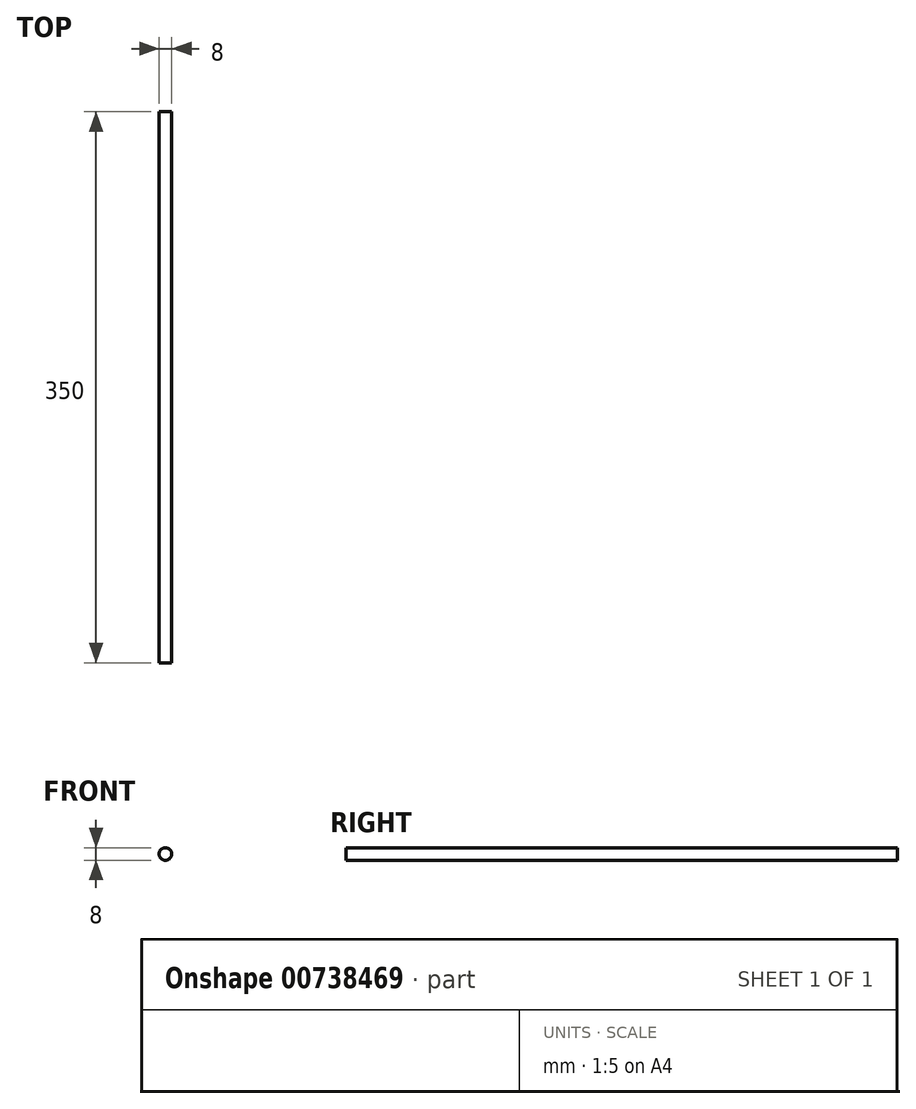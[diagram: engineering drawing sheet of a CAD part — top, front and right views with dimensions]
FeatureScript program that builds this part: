
annotation { "Feature Type Name" : "Feature", "Feature Type Description" : "" }
export const myFeature = defineFeature(function(context is Context, id is Id, definition is map)
    precondition{}
    {
        {
            var Q0;
            Q0=qCreatedBy(makeId("Front.planeOp"),FACE);
            var sketch = newSketch(context, id + "F0", { "sketchPlane" : qUnion([Q0])});
            skCircle(sketch, "E0", {"center": v(0, 0) * mm, "radius": 4 * mm});
            skSolve(sketch);
        }
        {
            var Q0;
            Q0=makeQuery(id+"F0.imprint","IMPRINT",FACE,{"disambiguationData":[TD([[makeQuery(id+"F0.imprint","IMPRINT",EDGE,{"derivedFrom":sQuery(id+"F0.wireOp",EDGE,"E0")}),1.0]])]});
            extrude(context, id + "F1", {"entities" : qUnion([Q0]), "endBound" : BoundingType.SYMMETRIC, "depth" : 350 * mm, "offsetDistance" : 25 * mm});
        }
    });
